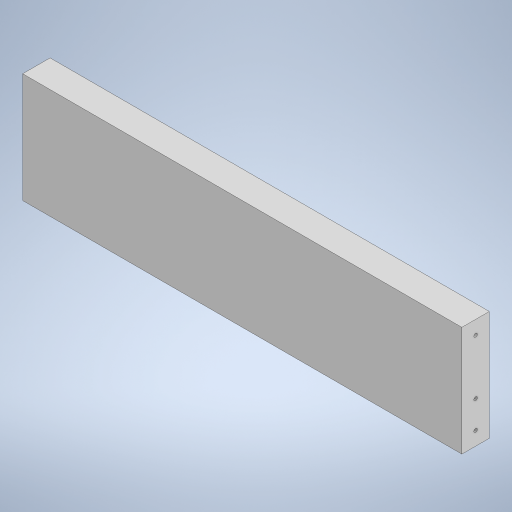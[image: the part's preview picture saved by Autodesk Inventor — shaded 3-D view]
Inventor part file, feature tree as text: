
AUTODESK INVENTOR PART (.ipt)
format: ipt  version: 2023 (Build 270158000, 158)  size: 321,024 bytes
history: native  units: in
note: dims shown in document units (in); Inventor stores cm internally (conversion verified against a paired STEP export)
features: extrude x5, sketch x5
ambient origin geometry x8: Origin, YZ Plane, XZ Plane, XY Plane, X Axis, Y Axis, Z Axis, Center Point
bodies: Solid1 (feature_tree)
feature tree (10):
  extrude  "Extrusion1"  Depth=54.0in
  extrude  "Extrusion2"  Depth=1.0in
  extrude  "Extrusion3"  Depth=16.0in
  extrude  "Extrusion4"  Depth=16.0in
  extrude  "Extrusion5"  Depth=1.0in
  sketch  "Sketch1"  dims[d0=54.0in d1=54.0in]
  sketch  "Sketch2"  dims[d2=1.0in d3=1.0in]
  sketch  "Sketch3"  dims[d4=8.0in d5=16.0in]
  sketch  "Sketch4"  dims[d6=8.0in d7=16.0in]
  sketch  "Sketch5"  dims[d8=16.0in d9=8.0in d10=16.0in d11=8.0in d12=4.0in d13=4.0in d14=4.0in d15=4.0in d16=17.0in d17=17.0in d18=17.0in d19=17.0in d20=20.0in d21=1.0in d22=1.0in d23=1.0in d24=1.0in d25=45.0deg d26=2.5in d27=45.0deg d28=45.0deg d29=45.0deg d30=1.0in d31=1.0in d32=1.0in d33=1.0in d34=0.25in d35=0.25in d36=0.25in d37=0.25in d38=0.25in d39=0.25in d40=0.25in d41=0.25in d42=4.0in d43=0.0in d44=0.125in d45=0.125in d46=0.5in d47=0.5in d48=0.5in d49=2.5in d50=1.0in d51=0.0in d52=0.125in d53=0.125in d54=0.5in d55=0.5in d56=0.5in d57=2.5in d58=1.0in d59=0.0in d60=0.125in d61=0.5in d62=0.5in d63=1.0in d64=0.0in d65=0.125in d66=0.5in d67=0.5in d68=1.0in d69=0.0in]
